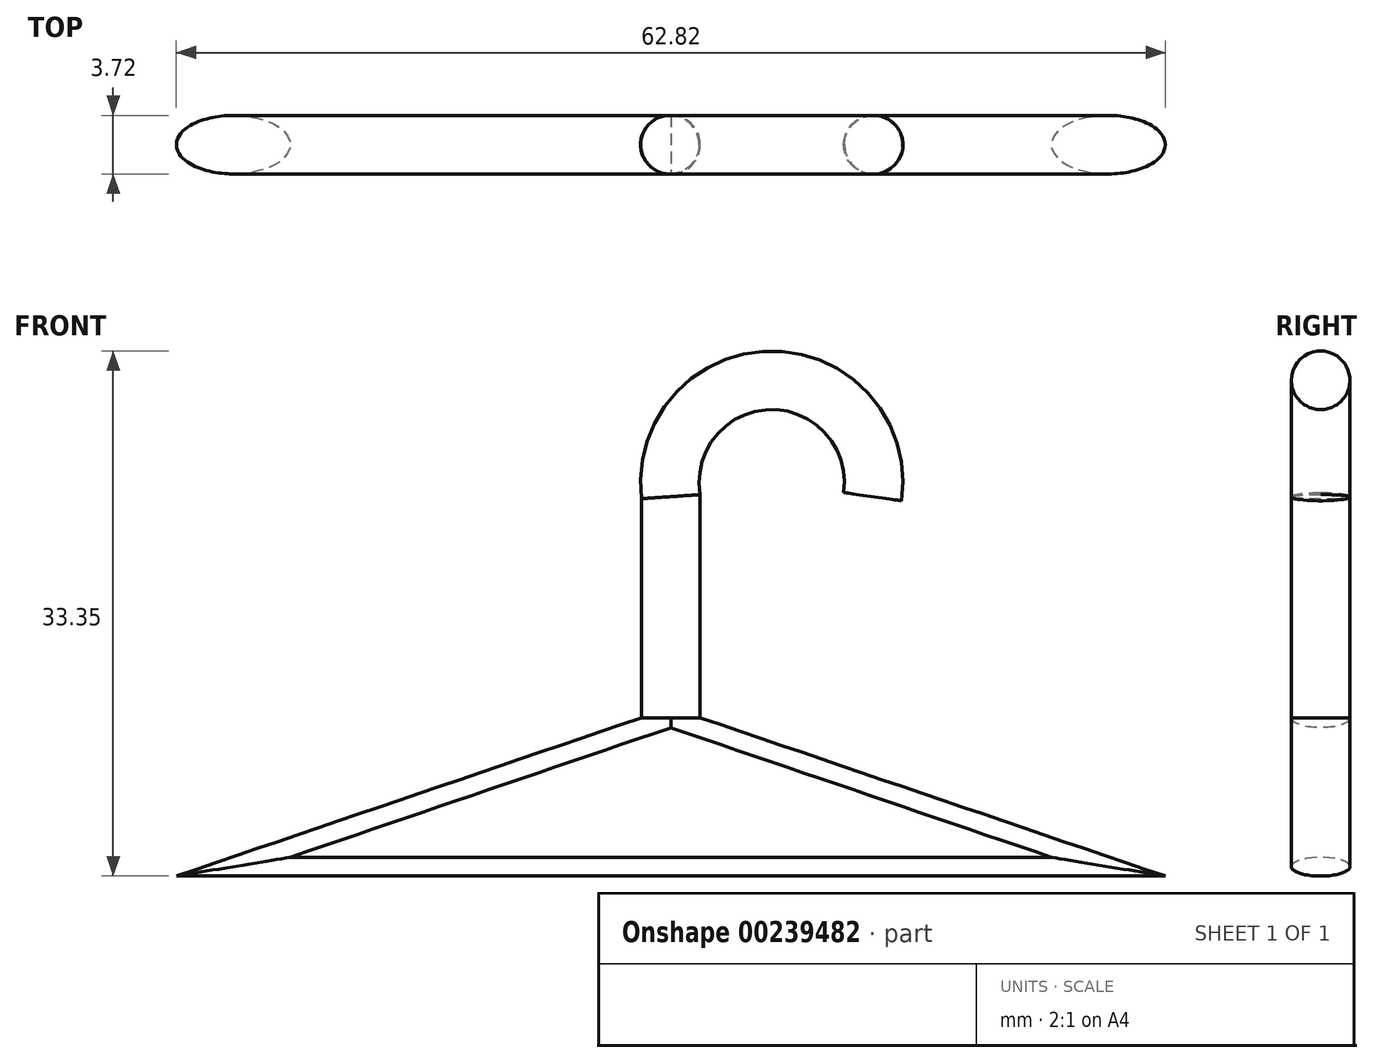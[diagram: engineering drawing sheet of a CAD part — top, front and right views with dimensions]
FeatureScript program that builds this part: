
annotation { "Feature Type Name" : "Feature", "Feature Type Description" : "" }
export const myFeature = defineFeature(function(context is Context, id is Id, definition is map)
    precondition{}
    {
        {
            var Q0;
            Q0=qCreatedBy(makeId("Front.planeOp"),FACE);
            var sketch = newSketch(context, id + "F0", { "sketchPlane" : qUnion([Q0])});
            skLineSegment(sketch, "E0", {"start": v(0, 0) * mm, "end": v(0, 14.04) * mm});
            skArc(sketch, "E1", {"start": v(12.82, 14.04) * mm, "mid": v(6.41, 21.43) * mm, "end": v(0, 14.04) * mm});
            skSolve(sketch);
        }
        {
            var Q0;
            Q0=qCreatedBy(makeId("Top.planeOp"),FACE);
            var sketch = newSketch(context, id + "F1", { "sketchPlane" : qUnion([Q0])});
            skCircle(sketch, "E2", {"center": v(0, 0) * mm, "radius": 1.86 * mm});
            skSolve(sketch);
        }
        {
            var Q0;
            Q0 = qSketchRegion(id + "F1", true);
            var Q1;
            Q1 = qConstructionFilter(qBodyType(qCreatedBy(id + "F0" ,EDGE), BodyType.WIRE), ConstructionObject.NO);
            sweep(context, id + "F2", {"profiles" : qUnion([Q0]), "path" : qUnion([Q1])});
        }
        {
            var Q0;
            Q0=qCreatedBy(makeId("Front.planeOp"),FACE);
            var sketch = newSketch(context, id + "F3", { "sketchPlane" : qUnion([Q0])});
            skLineSegment(sketch, "E3", {"start": v(0, 0) * mm, "end": v(27.79, -9.46) * mm});
            skLineSegment(sketch, "E4", {"start": v(27.79, -9.46) * mm, "end": v(-27.79, -9.46) * mm});
            skLineSegment(sketch, "E5", {"start": v(-27.79, -9.46) * mm, "end": v(0, 0) * mm});
            skSolve(sketch);
        }
        {
            var Q0;
            Q0 = qSketchRegion(id + "F1", true);
            var Q1;
            Q1 = qConstructionFilter(qBodyType(qCreatedBy(id + "F3" ,EDGE), BodyType.WIRE), ConstructionObject.NO);
            sweep(context, id + "F4", {"operationType" : NewBodyOperationType.ADD, "profiles" : qUnion([Q0]), "path" : qUnion([Q1])});
        }
    });
